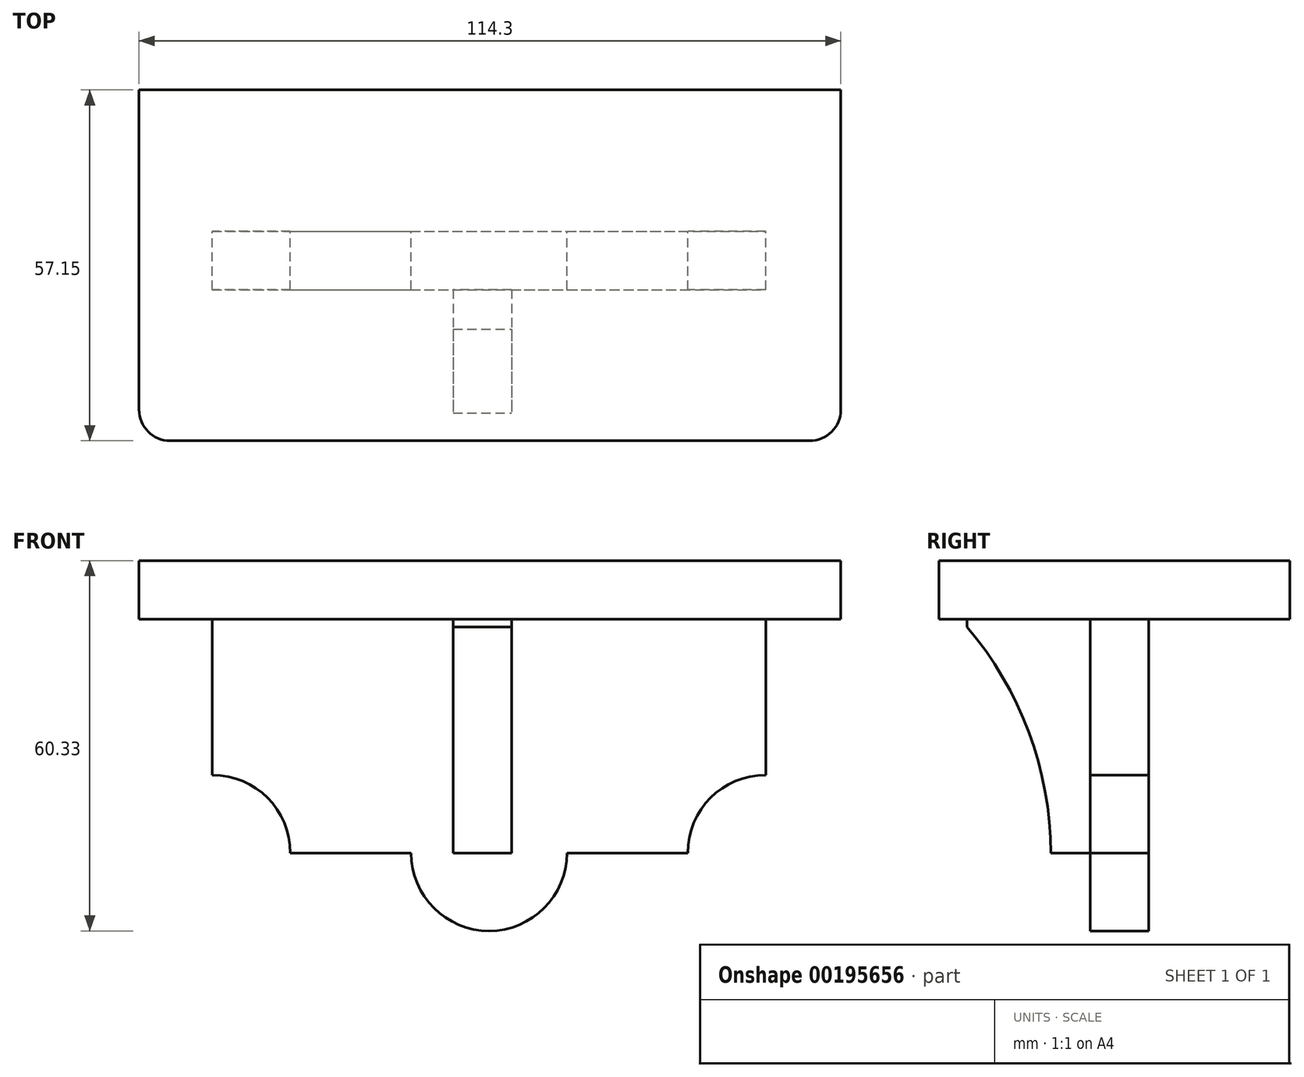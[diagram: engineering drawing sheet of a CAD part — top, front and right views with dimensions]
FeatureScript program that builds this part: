
annotation { "Feature Type Name" : "Feature", "Feature Type Description" : "" }
export const myFeature = defineFeature(function(context is Context, id is Id, definition is map)
    precondition{}
    {
        {
            var Q0;
            Q0=qCreatedBy(makeId("Top.planeOp"),FACE);
            var sketch = newSketch(context, id + "F0", { "sketchPlane" : qUnion([Q0])});
            skLineSegment(sketch, "E0.bottom", {"start": v(-60.69, 23.01) * mm, "end": v(53.61, 23.01) * mm});
            skLineSegment(sketch, "E0.top", {"start": v(-60.69, -34.14) * mm, "end": v(53.61, -34.14) * mm});
            skLineSegment(sketch, "E0.left", {"start": v(-60.69, 23.01) * mm, "end": v(-60.69, -34.14) * mm});
            skLineSegment(sketch, "E0.right", {"start": v(53.61, 23.01) * mm, "end": v(53.61, -34.14) * mm});
            skSolve(sketch);
        }
        {
            var Q0;
            Q0=makeQuery(id+"F0.imprint","IMPRINT",FACE,{"disambiguationData":[TD([[makeQuery(id+"F0.imprint","IMPRINT",EDGE,{"derivedFrom":sQuery(id+"F0.wireOp",EDGE,"E0.bottom")}),-1.0]])]});
            extrude(context, id + "F1", {"entities" : qUnion([Q0]), "depth" : 9.52 * mm});
        }
        {
            var Q0;
            Q0=makeQuery(id+"F1.opExtrude","SWEPT_EDGE",EDGE,{"disambiguationData":[OSD([sQuery(id+"F0.wireOp",EDGE,"E0.top"),sQuery(id+"F0.wireOp",EDGE,"E0.left")])]});
            var Q1;
            Q1=makeQuery(id+"F1.opExtrude","SWEPT_EDGE",EDGE,{"disambiguationData":[OSD([sQuery(id+"F0.wireOp",EDGE,"E0.top"),sQuery(id+"F0.wireOp",EDGE,"E0.right")])]});
            fillet(context, id + "F2", {"entities" : qUnion([Q0, Q1]), "radius" : 5.08 * mm, "tangentPropagation" : true, "allowEdgeOverflow" : false});
        }
        {
            var Q0;
            Q0=qCreatedBy(makeId("Front.planeOp"),FACE);
            var sketch = newSketch(context, id + "F3", { "sketchPlane" : qUnion([Q0])});
            skLineSegment(sketch, "E1.bottom", {"start": v(-48.74, 0) * mm, "end": v(41.38, 0) * mm});
            skLineSegment(sketch, "E1.top", {"start": v(-36.04, -38.1) * mm, "end": v(-16.38, -38.1) * mm});
            skLineSegment(sketch, "E1.left", {"start": v(-48.74, 0) * mm, "end": v(-48.74, -25.4) * mm});
            skLineSegment(sketch, "E1.right", {"start": v(41.38, 0) * mm, "end": v(41.38, -25.4) * mm});
            skArc(sketch, "E2", {"start": v(-16.38, -38.1) * mm, "mid": v(-3.68, -50.8) * mm, "end": v(9.02, -38.1) * mm});
            skArc(sketch, "E3", {"start": v(41.38, -25.4) * mm, "mid": v(32.4, -29.12) * mm, "end": v(28.68, -38.1) * mm});
            skArc(sketch, "E4", {"start": v(-36.04, -38.1) * mm, "mid": v(-39.76, -29.12) * mm, "end": v(-48.74, -25.4) * mm});
            skLineSegment(sketch, "E5.trimOffspring", {"start": v(9.02, -38.1) * mm, "end": v(28.68, -38.1) * mm});
            skSolve(sketch);
        }
        {
            var Q0;
            Q0=makeQuery(id+"F3.imprint","IMPRINT",FACE,{"disambiguationData":[TD([[makeQuery(id+"F3.imprint","IMPRINT",EDGE,{"derivedFrom":sQuery(id+"F3.wireOp",EDGE,"E1.bottom")}),-1.0]])]});
            extrude(context, id + "F4", {"entities" : qUnion([Q0]), "operationType" : NewBodyOperationType.ADD, "depth" : 9.52 * mm});
        }
        {
            var Q0;
            Q0=qCreatedBy(makeId("Right.planeOp"),FACE);
            var sketch = newSketch(context, id + "F5", { "sketchPlane" : qUnion([Q0])});
            skLineSegment(sketch, "E6.bottom", {"start": v(-9.29, 0) * mm, "end": v(-29.6, 0) * mm});
            skLineSegment(sketch, "E6.top", {"start": v(-9.29, -38.1) * mm, "end": v(-15.94, -38.1) * mm});
            skLineSegment(sketch, "E6.left", {"start": v(-9.29, 0) * mm, "end": v(-9.29, -38.1) * mm});
            skLineSegment(sketch, "E6.right", {"start": v(-29.6, 0) * mm, "end": v(-29.6, -1.3) * mm});
            skArc(sketch, "E7", {"start": v(-15.94, -38.1) * mm, "mid": v(-19.5, -18.48) * mm, "end": v(-29.6, -1.3) * mm});
            skPoint(sketch, "E8.start.orphan", {"position": v(-36.5, 0) * mm});
            skSolve(sketch);
        }
        {
            var Q0;
            Q0=makeQuery(id+"F5.imprint","IMPRINT",FACE,{"disambiguationData":[TD([[makeQuery(id+"F5.imprint","IMPRINT",EDGE,{"derivedFrom":sQuery(id+"F5.wireOp",EDGE,"E6.bottom")}),1.0]])]});
            extrude(context, id + "F6", {"entities" : qUnion([Q0]), "operationType" : NewBodyOperationType.ADD, "oppositeDirection" : true, "depth" : 9.52 * mm});
        }
    });
